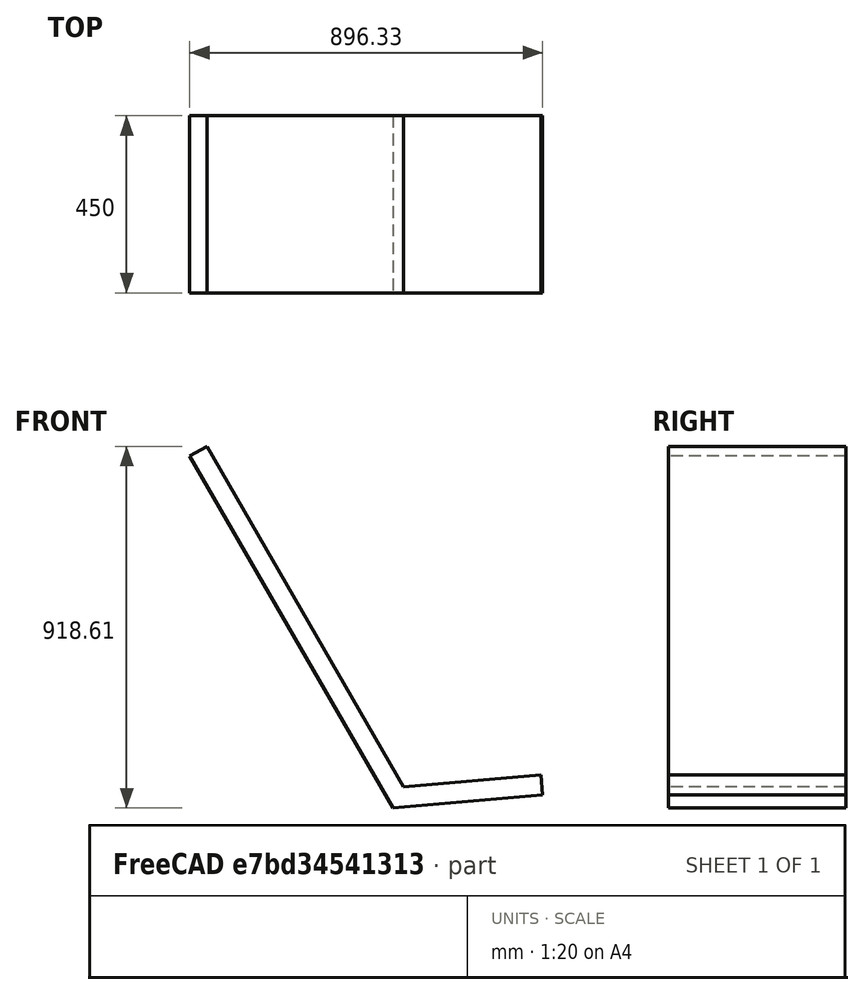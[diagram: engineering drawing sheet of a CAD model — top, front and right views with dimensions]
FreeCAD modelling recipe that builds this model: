
FCSTD DOCUMENT  (FreeCAD 0.20R29177 +426 (Git))
Label: seat
License: All rights reserved
LicenseURL: http://en.wikipedia.org/wiki/All_rights_reserved
objects: Sketcher::SketchObject×1, PartDesign::Pad×1, PartDesign::Body×1
note: 4 computed .brp shape members not serialized (recipe doc carries the construction recipe); baked Part::Feature solids carry a one-line shape summary decoded from their .brp

FEATURE [Sketcher::SketchObject] Sketch
  FullyConstrained = true
  MapMode = 5
  Placement = pos=(0,0,0) rot=(1,0,0;1.5708rad)
  Support = -> [XZ_Plane]
  sketch-geometry (6):
    g0: LineSegment StartX=376.043 StartY=83.0905 StartZ=0 EndX=27.3745 EndY=52.586 EndZ=0
    g1: LineSegment StartX=27.3745 StartY=52.586 StartZ=0 EndX=-472.625 EndY=918.611 EndZ=0
    g2: LineSegment StartX=-472.625 StartY=918.611 StartZ=0 EndX=-515.927 EndY=893.611 EndZ=0
    g3: LineSegment StartX=-515.927 StartY=893.611 StartZ=0 EndX=0 EndY=0 EndZ=0
    g4: LineSegment StartX=0 StartY=0 StartZ=0 EndX=380.4 EndY=33.2807 EndZ=0
    g5: LineSegment StartX=380.4 StartY=33.2807 StartZ=0 EndX=376.043 EndY=83.0905 EndZ=0
  constraints (17):
    c: Coincident(g0,g1)
    c: Coincident(g1,g2)
    c: Coincident(g2,g3)
    c: Coincident(g3,g-1)
    c: Coincident(g3,g4)
    c: Coincident(g4,g5)
    c: Coincident(g5,g0)
    c: Parallel(g4,g0)
    c: Parallel(g3,g1)
    c: Perpendicular(g3,g2)
    c: Perpendicular(g5,g0)
    c: Distance(g5) = 50
    c: Angle(g-1,g4) = 0.0872665
    c: Angle(g-1,g3) = 2.0944
    c: Distance(g0) = 350
    c: Distance(g1) = 1000
    c: Equal(g5,g2)
FEATURE [PartDesign::Pad] Pad
  Direction = (0,-1,-2e-16)
  Length = 450
  Length2 = 10
  Placement = pos=(0,0,0) rot=(1,0,0;1.5708rad)
  Profile = -> Sketch
  ReferenceAxis = -> Sketch [N_Axis]
  Refine = true
  Type = 0
FEATURE [PartDesign::Body] Body
  Group = -> [Sketch,Pad]
  Origin = -> Origin
  Tip = -> Pad
